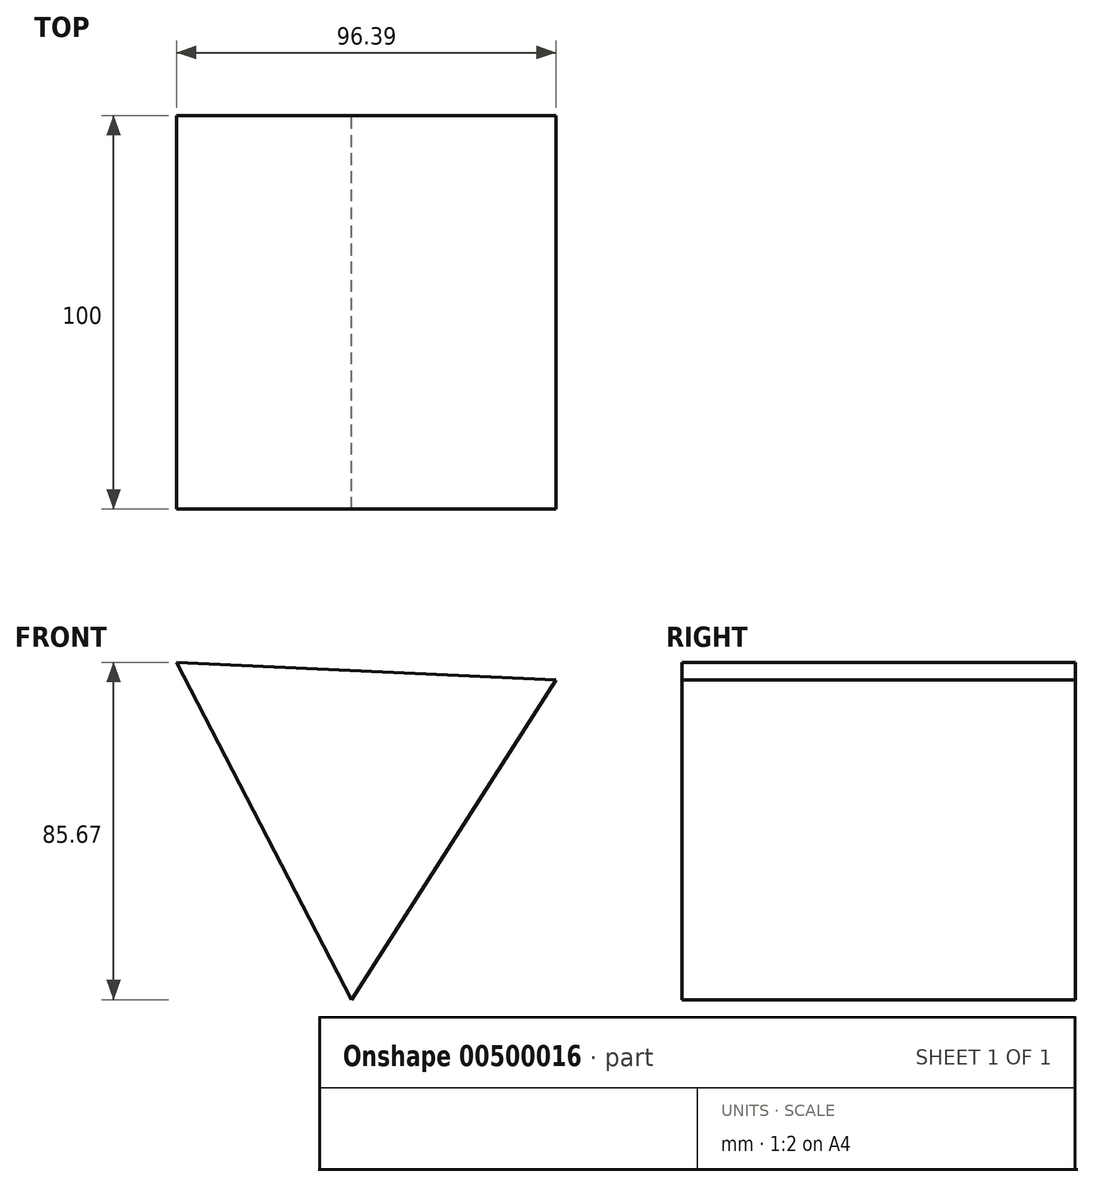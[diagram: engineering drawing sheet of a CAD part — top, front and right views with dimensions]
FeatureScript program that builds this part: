
annotation { "Feature Type Name" : "Feature", "Feature Type Description" : "" }
export const myFeature = defineFeature(function(context is Context, id is Id, definition is map)
    precondition{}
    {
        {
            var Q0;
            Q0=qCreatedBy(makeId("Front.planeOp"),FACE);
            var sketch = newSketch(context, id + "F0", { "sketchPlane" : qUnion([Q0])});
            skCircle(sketch, "E0.cCircle", {"center": v(0, -0.73) * mm, "radius": 55.7 * mm, "construction": true});
            skLineSegment(sketch, "E0.0", {"start": v(-46.93, 29.3) * mm, "end": v(49.46, 24.9) * mm});
            skLineSegment(sketch, "E0.1", {"start": v(49.46, 24.9) * mm, "end": v(-2.54, -56.38) * mm});
            skLineSegment(sketch, "E0.2", {"start": v(-2.54, -56.38) * mm, "end": v(-46.93, 29.3) * mm});
            skSolve(sketch);
        }
        {
            var Q0;
            Q0=makeQuery(id+"F0.imprint","IMPRINT",FACE,{"disambiguationData":[TD([[makeQuery(id+"F0.imprint","IMPRINT",EDGE,{"derivedFrom":sQuery(id+"F0.wireOp",EDGE,"E0.0")}),-1.0]])]});
            extrude(context, id + "F1", {"entities" : qUnion([Q0]), "endBound" : BoundingType.SYMMETRIC, "depth" : 100 * mm});
        }
    });
